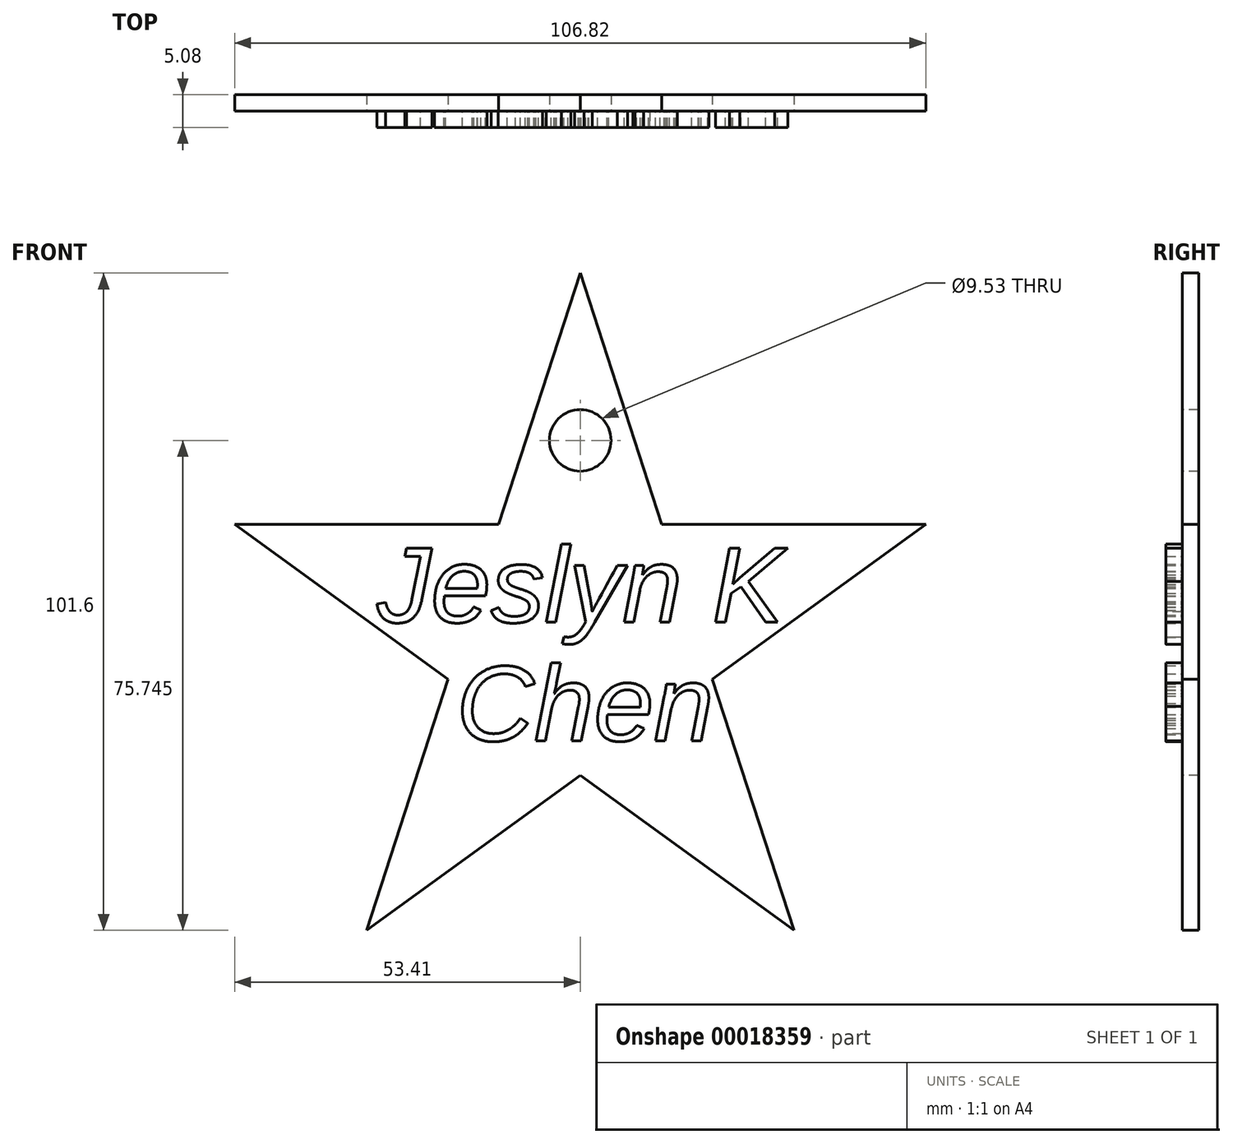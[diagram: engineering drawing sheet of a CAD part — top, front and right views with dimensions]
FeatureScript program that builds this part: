
annotation { "Feature Type Name" : "Feature", "Feature Type Description" : "" }
export const myFeature = defineFeature(function(context is Context, id is Id, definition is map)
    precondition{}
    {
        {
            var Q0;
            Q0=qCreatedBy(makeId("Front.planeOp"),FACE);
            var sketch = newSketch(context, id + "F0", { "sketchPlane" : qUnion([Q0])});
            skText(sketch, "E0", { "text": "Jeslyn K", "fontName": "Arimo-Italic.ttf"});
            skText(sketch, "E1", { "text": "Chen", "fontName": "Arimo-Italic.ttf"});
            skCircle(sketch, "E2", {"center": v(0, 51.77) * mm, "radius": 4.76 * mm});
            skLineSegment(sketch, "E3", {"start": v(-33.01, -23.98) * mm, "end": v(0, 77.62) * mm});
            skLineSegment(sketch, "E4", {"start": v(0, 77.62) * mm, "end": v(33.01, -23.98) * mm});
            skLineSegment(sketch, "E5", {"start": v(33.01, -23.98) * mm, "end": v(-53.41, 38.8) * mm});
            skLineSegment(sketch, "E6", {"start": v(-53.41, 38.8) * mm, "end": v(53.41, 38.8) * mm});
            skLineSegment(sketch, "E7", {"start": v(53.41, 38.8) * mm, "end": v(-33.01, -23.98) * mm});
            skPoint(sketch, "E8", {"position": v(0, 0) * mm});
            skPoint(sketch, "E9", {"position": v(0, 38.8) * mm});
            skLineSegment(sketch, "E10", {"start": v(-12.6, 38.8) * mm, "end": v(20.4, 14.82) * mm, "construction": true});
            skLineSegment(sketch, "E11", {"start": v(20.4, 14.82) * mm, "end": v(-20.4, 14.82) * mm, "construction": true});
            skLineSegment(sketch, "E12", {"start": v(0, 38.8) * mm, "end": v(0, 0) * mm, "construction": true});
            const initialGuessF0  = {"E0": [-0.03137, 0.02366, 1, 0, 0.01197], "E1": [-0.01912, 0.00533, 1, 0, 0.01197]};
            skSetInitialGuess(sketch, initialGuessF0);
            skSolve(sketch);
        }
        {
            var Q0;
            Q0 = qSketchRegion(id + "F0", true);
            var Q1;
            Q1=makeQuery(id+"F0.imprint","IMPRINT",FACE,{"disambiguationData":[TD([[makeQuery(id+"F0.imprint","IMPRINT",EDGE,{"derivedFrom":sQuery(id+"F0.wireOp",EDGE,"E0.sketch_text.stroke-107")}),1.0]])]});
            var Q2;
            {var subQ10=sQuery(id+"F0.wireOp",EDGE,"E1.sketch_text.stroke-1");Q2=makeQuery(id+"F0.imprint","IMPRINT",FACE,{"disambiguationData":[TD([[makeQuery(id+"F0.imprint","IMPRINT",EDGE,{"derivedFrom":subQ10}),1.0]])]});}
            var Q3;
            Q3=makeQuery(id+"F0.imprint","IMPRINT",FACE,{"disambiguationData":[TD([[makeQuery(id+"F0.imprint","IMPRINT",EDGE,{"derivedFrom":sQuery(id+"F0.wireOp",EDGE,"E0.sketch_text.stroke-0")}),1.0]])]});
            var Q4;
            Q4=makeQuery(id+"F0.imprint","IMPRINT",FACE,{"disambiguationData":[TD([[makeQuery(id+"F0.imprint","IMPRINT",EDGE,{"derivedFrom":sQuery(id+"F0.wireOp",EDGE,"E2")}),-1.0]])]});
            var Q5;
            {var subQ30=sQuery(id+"F0.wireOp",EDGE,"E0.sketch_text.stroke-19");Q5=makeQuery(id+"F0.imprint","IMPRINT",FACE,{"disambiguationData":[TD([[makeQuery(id+"F0.imprint","IMPRINT",EDGE,{"derivedFrom":subQ30}),1.0]])]});}
            var Q6;
            Q6=makeQuery(id+"F0.imprint","IMPRINT",FACE,{"disambiguationData":[TD([[makeQuery(id+"F0.imprint","IMPRINT",EDGE,{"derivedFrom":sQuery(id+"F0.wireOp",EDGE,"E1.sketch_text.stroke-63")}),1.0]])]});
            var Q7;
            {var subQ11=sQuery(id+"F0.wireOp",EDGE,"E1.sketch_text.stroke-66");Q7=makeQuery(id+"F0.imprint","IMPRINT",FACE,{"disambiguationData":[TD([[makeQuery(id+"F0.imprint","IMPRINT",EDGE,{"derivedFrom":subQ11}),-1.0]])]});}
            var Q8;
            {var subQ6=sQuery(id+"F0.wireOp",EDGE,"E0.sketch_text.stroke-14");Q8=makeQuery(id+"F0.imprint","IMPRINT",FACE,{"disambiguationData":[TD([[makeQuery(id+"F0.imprint","IMPRINT",EDGE,{"derivedFrom":subQ6}),1.0]])]});}
            var Q9;
            Q9=makeQuery(id+"F0.imprint","IMPRINT",FACE,{"disambiguationData":[TD([[makeQuery(id+"F0.imprint","IMPRINT",EDGE,{"derivedFrom":sQuery(id+"F0.wireOp",EDGE,"E1.sketch_text.stroke-21")}),-1.0]])]});
            var Q10;
            Q10=makeQuery(id+"F0.imprint","IMPRINT",FACE,{"disambiguationData":[TD([[makeQuery(id+"F0.imprint","IMPRINT",EDGE,{"derivedFrom":sQuery(id+"F0.wireOp",EDGE,"E0.sketch_text.stroke-107")}),-1.0]])]});
            var Q11;
            Q11=makeQuery(id+"F0.imprint","IMPRINT",FACE,{"disambiguationData":[TD([[makeQuery(id+"F0.imprint","IMPRINT",EDGE,{"derivedFrom":sQuery(id+"F0.wireOp",EDGE,"E0.sketch_text.stroke-87")}),-1.0]])]});
            var Q12;
            Q12=makeQuery(id+"F0.imprint","IMPRINT",FACE,{"disambiguationData":[TD([[makeQuery(id+"F0.imprint","IMPRINT",EDGE,{"derivedFrom":sQuery(id+"F0.wireOp",EDGE,"E0.sketch_text.stroke-69")}),-1.0]])]});
            var Q13;
            Q13=makeQuery(id+"F0.imprint","IMPRINT",FACE,{"disambiguationData":[TD([[makeQuery(id+"F0.imprint","IMPRINT",EDGE,{"derivedFrom":sQuery(id+"F0.wireOp",EDGE,"E1.sketch_text.stroke-40")}),-1.0]])]});
            var Q14;
            Q14=makeQuery(id+"F0.imprint","IMPRINT",FACE,{"disambiguationData":[TD([[makeQuery(id+"F0.imprint","IMPRINT",EDGE,{"derivedFrom":sQuery(id+"F0.wireOp",EDGE,"E0.sketch_text.stroke-65")}),-1.0]])]});
            var Q15;
            Q15=makeQuery(id+"F0.imprint","IMPRINT",FACE,{"disambiguationData":[TD([[makeQuery(id+"F0.imprint","IMPRINT",EDGE,{"derivedFrom":sQuery(id+"F0.wireOp",EDGE,"E0.sketch_text.stroke-37")}),-1.0]])]});
            var Q16;
            Q16=makeQuery(id+"F0.imprint","IMPRINT",FACE,{"disambiguationData":[TD([[makeQuery(id+"F0.imprint","IMPRINT",EDGE,{"derivedFrom":sQuery(id+"F0.wireOp",EDGE,"E0.sketch_text.stroke-0")}),-1.0]])]});
            var Q17;
            {var subQ10=sQuery(id+"F0.wireOp",EDGE,"E1.sketch_text.stroke-1");Q17=makeQuery(id+"F0.imprint","IMPRINT",FACE,{"disambiguationData":[TD([[makeQuery(id+"F0.imprint","IMPRINT",EDGE,{"derivedFrom":subQ10}),-1.0]])]});}
            var Q18;
            {var subQ5=sQuery(id+"F0.wireOp",EDGE,"E1.sketch_text.stroke-69");Q18=makeQuery(id+"F0.imprint","IMPRINT",FACE,{"disambiguationData":[TD([[makeQuery(id+"F0.imprint","IMPRINT",EDGE,{"derivedFrom":subQ5}),-1.0]])]});}
            var Q19;
            {var subQ7=sQuery(id+"F0.wireOp",EDGE,"E0.sketch_text.stroke-14");Q19=makeQuery(id+"F0.imprint","IMPRINT",FACE,{"disambiguationData":[TD([[makeQuery(id+"F0.imprint","IMPRINT",EDGE,{"derivedFrom":subQ7}),-1.0]])]});}
            var Q20;
            Q20=makeQuery(id+"F0.imprint","IMPRINT",FACE,{"disambiguationData":[TD([[makeQuery(id+"F0.imprint","IMPRINT",EDGE,{"derivedFrom":sQuery(id+"F0.wireOp",EDGE,"E1.sketch_text.stroke-63")}),-1.0]])]});
            var Q21;
            {var subQ1=sQuery(id+"F0.wireOp",EDGE,"E1.sketch_text.stroke-47");var subQ3=sQuery(id+"F0.wireOp",EDGE,"E1.sketch_text.stroke-46");var subQ5=makeQuery(id+"F0.imprint","INTERSECT",VERTEX,{"derivedFrom":[subQ3,subQ1]});Q21=makeQuery(id+"F0.imprint","IMPRINT",FACE,{"disambiguationData":[TD([[makeQuery(id+"F0.imprint","IMPRINT",EDGE,{"disambiguationData":[TD([[subQ5,1.0]])],"derivedFrom":subQ3}),-1.0]])]});}
            var Q22;
            {var subQ6=sQuery(id+"F0.wireOp",EDGE,"E1.sketch_text.stroke-16");Q22=makeQuery(id+"F0.imprint","IMPRINT",FACE,{"disambiguationData":[TD([[makeQuery(id+"F0.imprint","IMPRINT",EDGE,{"derivedFrom":subQ6}),1.0]])]});}
            var Q23;
            {var subQ6=sQuery(id+"F0.wireOp",EDGE,"E1.sketch_text.stroke-6");Q23=makeQuery(id+"F0.imprint","IMPRINT",FACE,{"disambiguationData":[TD([[makeQuery(id+"F0.imprint","IMPRINT",EDGE,{"derivedFrom":subQ6}),-1.0]])]});}
            var Q24;
            {var subQ5=sQuery(id+"F0.wireOp",EDGE,"E0.sketch_text.stroke-29");Q24=makeQuery(id+"F0.imprint","IMPRINT",FACE,{"disambiguationData":[TD([[makeQuery(id+"F0.imprint","IMPRINT",EDGE,{"derivedFrom":subQ5}),-1.0]])]});}
            var Q25;
            {var subQ5=sQuery(id+"F0.wireOp",EDGE,"E0.sketch_text.stroke-19");Q25=makeQuery(id+"F0.imprint","IMPRINT",FACE,{"disambiguationData":[TD([[makeQuery(id+"F0.imprint","IMPRINT",EDGE,{"derivedFrom":subQ5}),-1.0]])]});}
            var Q26;
            Q26=makeQuery(id+"F0.imprint","IMPRINT",FACE,{"disambiguationData":[TD([[makeQuery(id+"F0.imprint","IMPRINT",EDGE,{"derivedFrom":sQuery(id+"F0.wireOp",EDGE,"E1.sketch_text.stroke-57")}),1.0]])]});
            var Q27;
            Q27=makeQuery(id+"F0.imprint","IMPRINT",FACE,{"disambiguationData":[TD([[makeQuery(id+"F0.imprint","IMPRINT",EDGE,{"derivedFrom":sQuery(id+"F0.wireOp",EDGE,"E0.sketch_text.stroke-31")}),1.0]])]});
            var Q28;
            {var subQ5=sQuery(id+"F0.wireOp",EDGE,"E1.sketch_text.stroke-20");Q28=makeQuery(id+"F0.imprint","IMPRINT",FACE,{"disambiguationData":[TD([[makeQuery(id+"F0.imprint","IMPRINT",EDGE,{"derivedFrom":subQ5}),-1.0]])]});}
            var Q29;
            {var subQ5=sQuery(id+"F0.wireOp",EDGE,"E1.sketch_text.stroke-66");Q29=makeQuery(id+"F0.imprint","IMPRINT",FACE,{"disambiguationData":[TD([[makeQuery(id+"F0.imprint","IMPRINT",EDGE,{"derivedFrom":subQ5}),1.0]])]});}
            extrude(context, id + "F1", {"entities" : qUnion([Q0, Q1, Q2, Q3, Q4, Q5, Q6, Q7, Q8, Q9, Q10, Q11, Q12, Q13, Q14, Q15, Q16, Q17, Q18, Q19, Q20, Q21, Q22, Q23, Q24, Q25, Q26, Q27, Q28, Q29]), "oppositeDirection" : true, "depth" : 2.54 * mm});
        }
        {
            var Q0;
            Q0=makeQuery(id+"F0.imprint","IMPRINT",FACE,{"disambiguationData":[TD([[makeQuery(id+"F0.imprint","IMPRINT",EDGE,{"derivedFrom":sQuery(id+"F0.wireOp",EDGE,"E0.sketch_text.stroke-0")}),-1.0]])]});
            var Q1;
            {var subQ7=sQuery(id+"F0.wireOp",EDGE,"E0.sketch_text.stroke-14");Q1=makeQuery(id+"F0.imprint","IMPRINT",FACE,{"disambiguationData":[TD([[makeQuery(id+"F0.imprint","IMPRINT",EDGE,{"derivedFrom":subQ7}),-1.0]])]});}
            var Q2;
            Q2=makeQuery(id+"F0.imprint","IMPRINT",FACE,{"disambiguationData":[TD([[makeQuery(id+"F0.imprint","IMPRINT",EDGE,{"derivedFrom":sQuery(id+"F0.wireOp",EDGE,"E0.sketch_text.stroke-37")}),-1.0]])]});
            var Q3;
            Q3=makeQuery(id+"F0.imprint","IMPRINT",FACE,{"disambiguationData":[TD([[makeQuery(id+"F0.imprint","IMPRINT",EDGE,{"derivedFrom":sQuery(id+"F0.wireOp",EDGE,"E0.sketch_text.stroke-65")}),-1.0]])]});
            var Q4;
            Q4=makeQuery(id+"F0.imprint","IMPRINT",FACE,{"disambiguationData":[TD([[makeQuery(id+"F0.imprint","IMPRINT",EDGE,{"derivedFrom":sQuery(id+"F0.wireOp",EDGE,"E0.sketch_text.stroke-69")}),-1.0]])]});
            var Q5;
            Q5=makeQuery(id+"F0.imprint","IMPRINT",FACE,{"disambiguationData":[TD([[makeQuery(id+"F0.imprint","IMPRINT",EDGE,{"derivedFrom":sQuery(id+"F0.wireOp",EDGE,"E0.sketch_text.stroke-87")}),-1.0]])]});
            var Q6;
            Q6=makeQuery(id+"F0.imprint","IMPRINT",FACE,{"disambiguationData":[TD([[makeQuery(id+"F0.imprint","IMPRINT",EDGE,{"derivedFrom":sQuery(id+"F0.wireOp",EDGE,"E0.sketch_text.stroke-107")}),-1.0]])]});
            var Q7;
            {var subQ6=sQuery(id+"F0.wireOp",EDGE,"E1.sketch_text.stroke-6");Q7=makeQuery(id+"F0.imprint","IMPRINT",FACE,{"disambiguationData":[TD([[makeQuery(id+"F0.imprint","IMPRINT",EDGE,{"derivedFrom":subQ6}),-1.0]])]});}
            var Q8;
            {var subQ10=sQuery(id+"F0.wireOp",EDGE,"E1.sketch_text.stroke-1");Q8=makeQuery(id+"F0.imprint","IMPRINT",FACE,{"disambiguationData":[TD([[makeQuery(id+"F0.imprint","IMPRINT",EDGE,{"derivedFrom":subQ10}),-1.0]])]});}
            var Q9;
            Q9=makeQuery(id+"F0.imprint","IMPRINT",FACE,{"disambiguationData":[TD([[makeQuery(id+"F0.imprint","IMPRINT",EDGE,{"derivedFrom":sQuery(id+"F0.wireOp",EDGE,"E1.sketch_text.stroke-21")}),-1.0]])]});
            var Q10;
            Q10=makeQuery(id+"F0.imprint","IMPRINT",FACE,{"disambiguationData":[TD([[makeQuery(id+"F0.imprint","IMPRINT",EDGE,{"derivedFrom":sQuery(id+"F0.wireOp",EDGE,"E1.sketch_text.stroke-40")}),-1.0]])]});
            var Q11;
            {var subQ11=sQuery(id+"F0.wireOp",EDGE,"E1.sketch_text.stroke-66");Q11=makeQuery(id+"F0.imprint","IMPRINT",FACE,{"disambiguationData":[TD([[makeQuery(id+"F0.imprint","IMPRINT",EDGE,{"derivedFrom":subQ11}),-1.0]])]});}
            var Q12;
            {var subQ5=sQuery(id+"F0.wireOp",EDGE,"E1.sketch_text.stroke-69");Q12=makeQuery(id+"F0.imprint","IMPRINT",FACE,{"disambiguationData":[TD([[makeQuery(id+"F0.imprint","IMPRINT",EDGE,{"derivedFrom":subQ5}),-1.0]])]});}
            var Q13;
            Q13=makeQuery(id+"F0.imprint","IMPRINT",FACE,{"disambiguationData":[TD([[makeQuery(id+"F0.imprint","IMPRINT",EDGE,{"derivedFrom":sQuery(id+"F0.wireOp",EDGE,"E1.sketch_text.stroke-63")}),-1.0]])]});
            var Q14;
            {var subQ5=sQuery(id+"F0.wireOp",EDGE,"E0.sketch_text.stroke-29");Q14=makeQuery(id+"F0.imprint","IMPRINT",FACE,{"disambiguationData":[TD([[makeQuery(id+"F0.imprint","IMPRINT",EDGE,{"derivedFrom":subQ5}),-1.0]])]});}
            var Q15;
            {var subQ5=sQuery(id+"F0.wireOp",EDGE,"E0.sketch_text.stroke-19");Q15=makeQuery(id+"F0.imprint","IMPRINT",FACE,{"disambiguationData":[TD([[makeQuery(id+"F0.imprint","IMPRINT",EDGE,{"derivedFrom":subQ5}),-1.0]])]});}
            var Q16;
            {var subQ5=sQuery(id+"F0.wireOp",EDGE,"E1.sketch_text.stroke-20");Q16=makeQuery(id+"F0.imprint","IMPRINT",FACE,{"disambiguationData":[TD([[makeQuery(id+"F0.imprint","IMPRINT",EDGE,{"derivedFrom":subQ5}),-1.0]])]});}
            var Q17;
            {var subQ1=sQuery(id+"F0.wireOp",EDGE,"E1.sketch_text.stroke-47");var subQ3=sQuery(id+"F0.wireOp",EDGE,"E1.sketch_text.stroke-46");var subQ5=makeQuery(id+"F0.imprint","INTERSECT",VERTEX,{"derivedFrom":[subQ3,subQ1]});Q17=makeQuery(id+"F0.imprint","IMPRINT",FACE,{"disambiguationData":[TD([[makeQuery(id+"F0.imprint","IMPRINT",EDGE,{"disambiguationData":[TD([[subQ5,1.0]])],"derivedFrom":subQ3}),-1.0]])]});}
            extrude(context, id + "F2", {"entities" : qUnion([Q0, Q1, Q2, Q3, Q4, Q5, Q6, Q7, Q8, Q9, Q10, Q11, Q12, Q13, Q14, Q15, Q16, Q17]), "operationType" : NewBodyOperationType.ADD, "depth" : 2.54 * mm});
        }
    });
